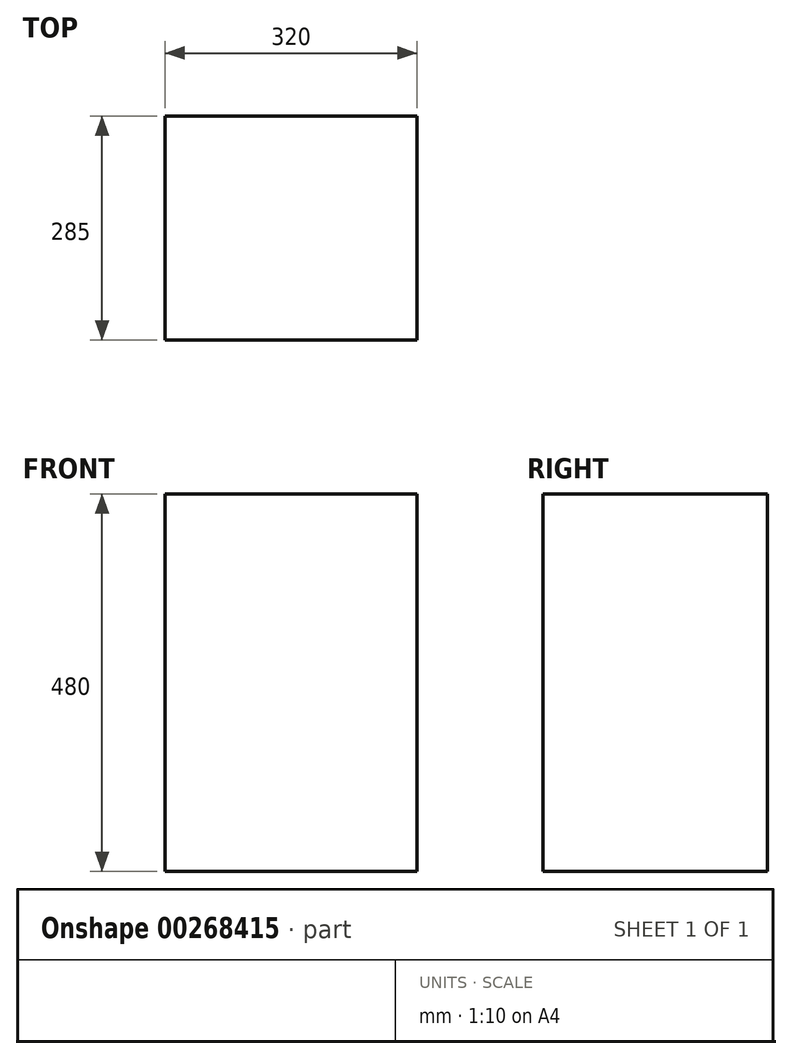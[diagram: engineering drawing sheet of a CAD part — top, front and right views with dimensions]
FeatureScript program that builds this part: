
annotation { "Feature Type Name" : "Feature", "Feature Type Description" : "" }
export const myFeature = defineFeature(function(context is Context, id is Id, definition is map)
    precondition{}
    {
        {
            var Q0;
            Q0=qCreatedBy(makeId("Top.planeOp"),FACE);
            var sketch = newSketch(context, id + "F0", { "sketchPlane" : qUnion([Q0])});
            skLineSegment(sketch, "E0.bottom", {"start": v(160, 142.5) * mm, "end": v(-160, 142.5) * mm});
            skLineSegment(sketch, "E0.top", {"start": v(160, -142.5) * mm, "end": v(-160, -142.5) * mm});
            skLineSegment(sketch, "E0.left", {"start": v(160, 142.5) * mm, "end": v(160, -142.5) * mm});
            skLineSegment(sketch, "E0.right", {"start": v(-160, 142.5) * mm, "end": v(-160, -142.5) * mm});
            skPoint(sketch, "E0.middle", {"position": v(0, 0) * mm});
            skSolve(sketch);
        }
        {
            var Q0;
            Q0=makeQuery(id+"F0.imprint","IMPRINT",FACE,{"disambiguationData":[TD([[makeQuery(id+"F0.imprint","IMPRINT",EDGE,{"derivedFrom":sQuery(id+"F0.wireOp",EDGE,"E0.bottom")}),1.0]])]});
            extrude(context, id + "F1", {"entities" : qUnion([Q0]), "depth" : 480 * mm});
        }
    });
